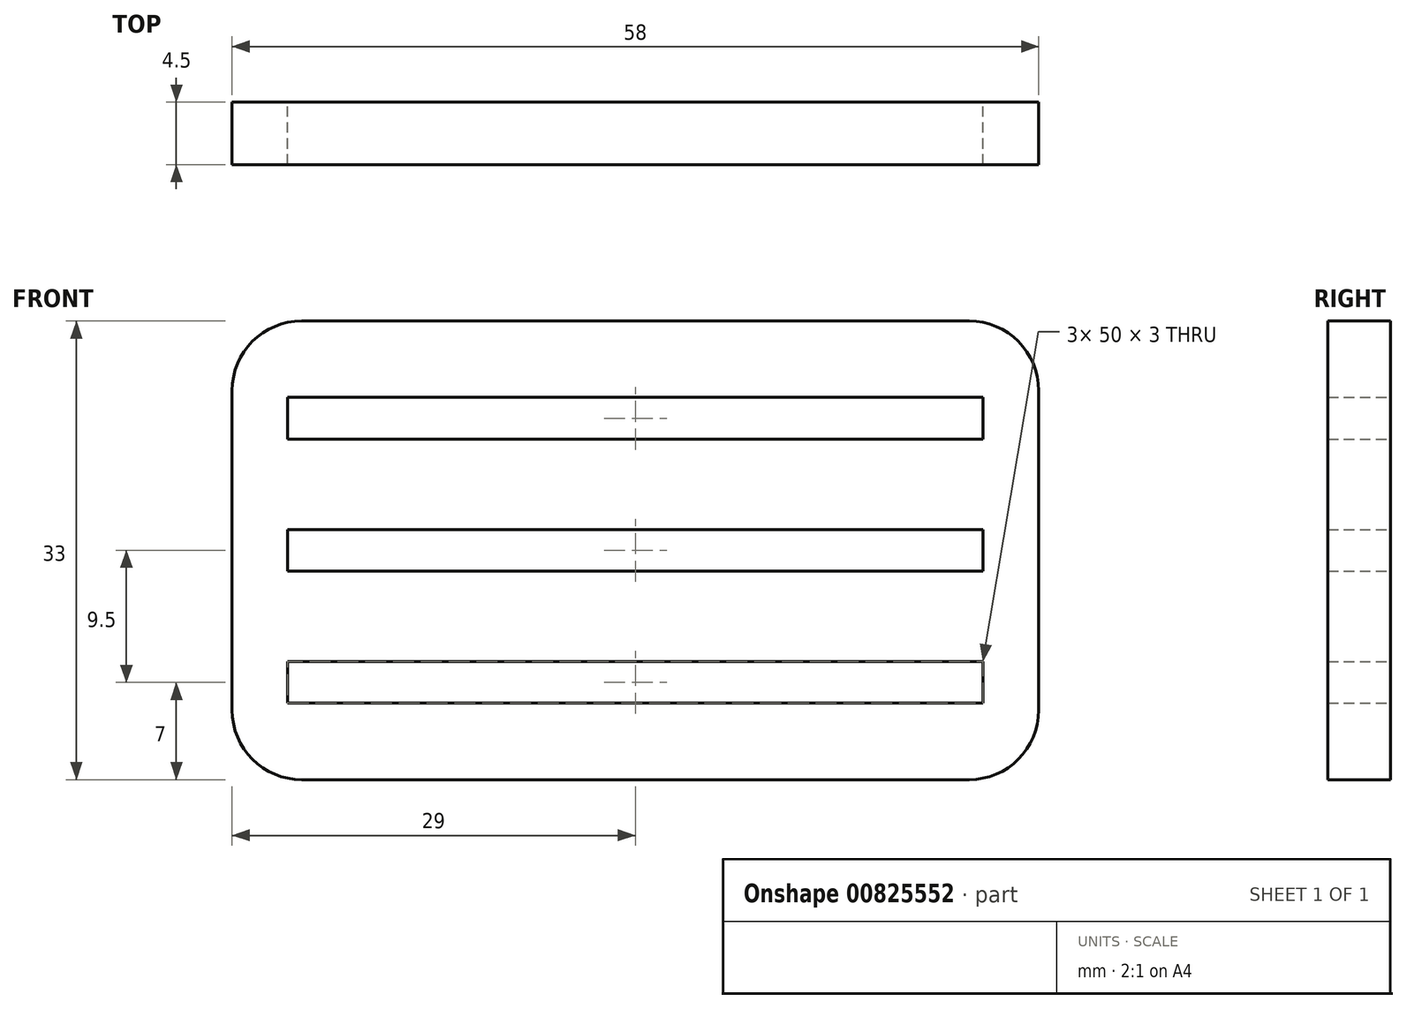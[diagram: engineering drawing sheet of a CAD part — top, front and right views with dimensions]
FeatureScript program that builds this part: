
annotation { "Feature Type Name" : "Feature", "Feature Type Description" : "" }
export const myFeature = defineFeature(function(context is Context, id is Id, definition is map)
    precondition{}
    {
        {
            var Q0;
            Q0=qCreatedBy(makeId("Front.planeOp"),FACE);
            var sketch = newSketch(context, id + "F0", { "sketchPlane" : qUnion([Q0])});
            skLineSegment(sketch, "E0.bottom", {"start": v(24, -16.5) * mm, "end": v(-24, -16.5) * mm});
            skLineSegment(sketch, "E0.top", {"start": v(24, 16.5) * mm, "end": v(-24, 16.5) * mm});
            skLineSegment(sketch, "E0.left", {"start": v(29, -11.5) * mm, "end": v(29, 11.5) * mm});
            skLineSegment(sketch, "E0.right", {"start": v(-29, -11.5) * mm, "end": v(-29, 11.5) * mm});
            skPoint(sketch, "E0.middle", {"position": v(0, 0) * mm});
            skPoint(sketch, "E1.visualSharp", {"position": v(-29, 16.5) * mm});
            skArc(sketch, "E1.filletArc", {"start": v(-24, 16.5) * mm, "mid": v(-27.54, 15.04) * mm, "end": v(-29, 11.5) * mm});
            skPoint(sketch, "E2.visualSharp", {"position": v(29, 16.5) * mm});
            skArc(sketch, "E2.filletArc", {"start": v(29, 11.5) * mm, "mid": v(27.54, 15.04) * mm, "end": v(24, 16.5) * mm});
            skPoint(sketch, "E3.visualSharp", {"position": v(29, -16.5) * mm});
            skArc(sketch, "E3.filletArc", {"start": v(24, -16.5) * mm, "mid": v(27.54, -15.04) * mm, "end": v(29, -11.5) * mm});
            skPoint(sketch, "E4.visualSharp", {"position": v(-29, -16.5) * mm});
            skArc(sketch, "E4.filletArc", {"start": v(-29, -11.5) * mm, "mid": v(-27.54, -15.04) * mm, "end": v(-24, -16.5) * mm});
            skSolve(sketch);
        }
        {
            var Q0;
            Q0=qCreatedBy(makeId("Front.planeOp"),FACE);
            var sketch = newSketch(context, id + "F1", { "sketchPlane" : qUnion([Q0])});
            skLineSegment(sketch, "E5.bottom", {"start": v(25, -1.5) * mm, "end": v(-25, -1.5) * mm});
            skLineSegment(sketch, "E5.top", {"start": v(25, 1.5) * mm, "end": v(-25, 1.5) * mm});
            skLineSegment(sketch, "E5.left", {"start": v(25, -1.5) * mm, "end": v(25, 1.5) * mm});
            skLineSegment(sketch, "E5.right", {"start": v(-25, -1.5) * mm, "end": v(-25, 1.5) * mm});
            skPoint(sketch, "E5.middle", {"position": v(0, 0) * mm});
            skLineSegment(sketch, "E6.bottom", {"start": v(25, 8) * mm, "end": v(-25, 8) * mm});
            skLineSegment(sketch, "E6.top", {"start": v(25, 11) * mm, "end": v(-25, 11) * mm});
            skLineSegment(sketch, "E6.left", {"start": v(25, 8) * mm, "end": v(25, 11) * mm});
            skLineSegment(sketch, "E6.right", {"start": v(-25, 8) * mm, "end": v(-25, 11) * mm});
            skPoint(sketch, "E6.middle", {"position": v(0, 9.5) * mm});
            skLineSegment(sketch, "E7.bottom", {"start": v(25, -11) * mm, "end": v(-25, -11) * mm});
            skLineSegment(sketch, "E7.top", {"start": v(25, -8) * mm, "end": v(-25, -8) * mm});
            skLineSegment(sketch, "E7.left", {"start": v(25, -11) * mm, "end": v(25, -8) * mm});
            skLineSegment(sketch, "E7.right", {"start": v(-25, -11) * mm, "end": v(-25, -8) * mm});
            skPoint(sketch, "E7.middle", {"position": v(0, -9.5) * mm});
            skSolve(sketch);
        }
        {
            var Q0;
            Q0=makeQuery(id+"F0.imprint","IMPRINT",FACE,{"disambiguationData":[TD([[makeQuery(id+"F0.imprint","IMPRINT",EDGE,{"derivedFrom":sQuery(id+"F0.wireOp",EDGE,"E0.bottom")}),-1.0]])]});
            extrude(context, id + "F2", {"entities" : qUnion([Q0]), "depth" : 4.5 * mm, "offsetDistance" : 25 * mm});
        }
        {
            var Q0;
            Q0 = qSketchRegion(id + "F1", true);
            extrude(context, id + "F3", {"entities" : qUnion([Q0]), "operationType" : NewBodyOperationType.REMOVE, "depth" : 4.5 * mm, "offsetDistance" : 25 * mm});
        }
    });
